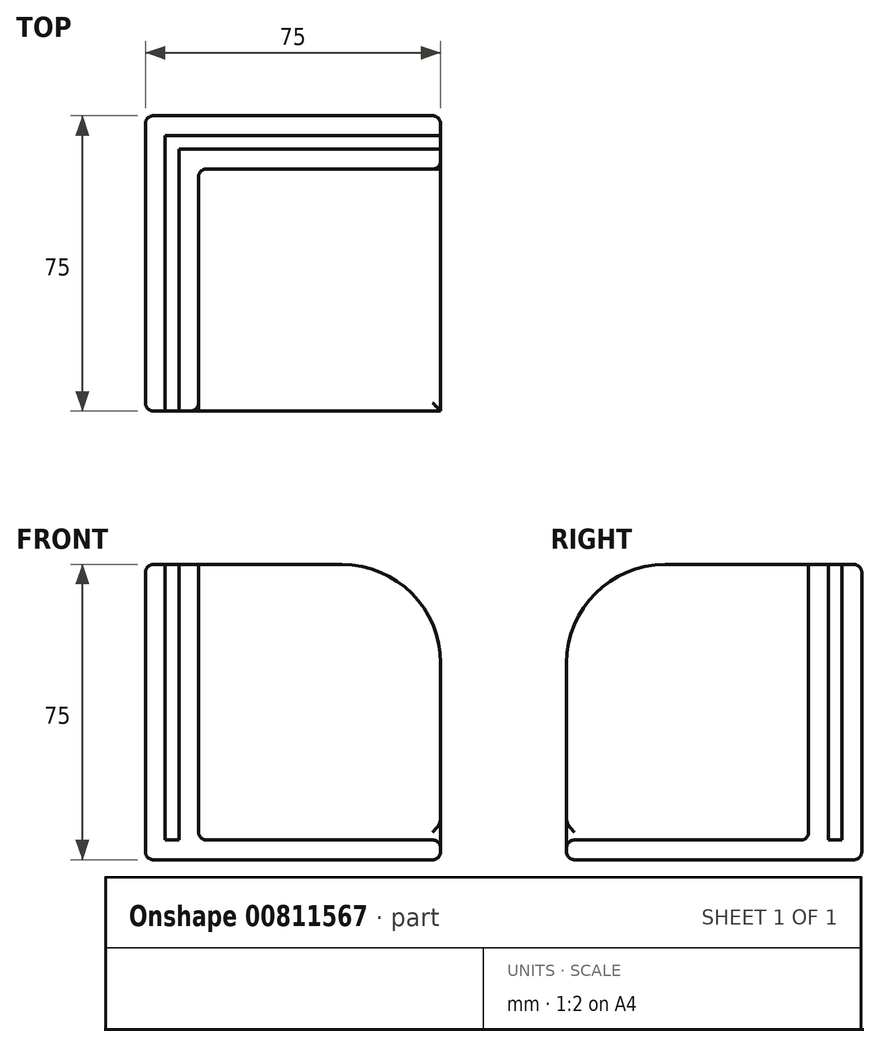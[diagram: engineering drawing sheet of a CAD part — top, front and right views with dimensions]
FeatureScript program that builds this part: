
annotation { "Feature Type Name" : "Feature", "Feature Type Description" : "" }
export const myFeature = defineFeature(function(context is Context, id is Id, definition is map)
    precondition{}
    {
        {
            var Q0;
            Q0=qCreatedBy(makeId("Top.planeOp"),FACE);
            var sketch = newSketch(context, id + "F0", { "sketchPlane" : qUnion([Q0])});
            skLineSegment(sketch, "E0.bottom", {"start": v(37.5, -37.5) * mm, "end": v(-37.5, -37.5) * mm});
            skLineSegment(sketch, "E0.top", {"start": v(37.5, 37.5) * mm, "end": v(-37.5, 37.5) * mm});
            skLineSegment(sketch, "E0.left", {"start": v(37.5, -37.5) * mm, "end": v(37.5, 37.5) * mm});
            skLineSegment(sketch, "E0.right", {"start": v(-37.5, -37.5) * mm, "end": v(-37.5, 37.5) * mm});
            skPoint(sketch, "E0.middle", {"position": v(0, 0) * mm});
            skSolve(sketch);
        }
        {
            var Q0;
            Q0 = qSketchRegion(id + "F0", true);
            extrude(context, id + "F1", {"entities" : qUnion([Q0]), "depth" : 5 * mm, "offsetDistance" : 25 * mm});
        }
        {
            var Q0;
            Q0=makeQuery(id+"F1.opExtrude","CAP_FACE",FACE,{"disambiguationData":[OSD([sQuery(id+"F0.wireOp",EDGE,"E0.bottom"),sQuery(id+"F0.wireOp",EDGE,"E0.top"),sQuery(id+"F0.wireOp",EDGE,"E0.left"),sQuery(id+"F0.wireOp",EDGE,"E0.right")])],"isStart":false});
            var sketch = newSketch(context, id + "F2", { "sketchPlane" : qUnion([Q0])});
            skLineSegment(sketch, "E1.bottom", {"start": v(-37.5, 37.5) * mm, "end": v(-32.5, 37.5) * mm});
            skLineSegment(sketch, "E1.top", {"start": v(-37.5, -37.5) * mm, "end": v(-32.5, -37.5) * mm});
            skLineSegment(sketch, "E1.left", {"start": v(-37.5, 37.5) * mm, "end": v(-37.5, -37.5) * mm});
            skLineSegment(sketch, "E1.right", {"start": v(-32.5, 37.5) * mm, "end": v(-32.5, -37.5) * mm});
            skLineSegment(sketch, "E2.bottom", {"start": v(-32.5, 37.5) * mm, "end": v(37.5, 37.5) * mm});
            skLineSegment(sketch, "E2.top", {"start": v(-32.5, 32.5) * mm, "end": v(37.5, 32.5) * mm});
            skLineSegment(sketch, "E2.left", {"start": v(-32.5, 37.5) * mm, "end": v(-32.5, 32.5) * mm});
            skLineSegment(sketch, "E2.right", {"start": v(37.5, 37.5) * mm, "end": v(37.5, 32.5) * mm});
            skSolve(sketch);
        }
        {
            var Q0;
            Q0 = qSketchRegion(id + "F2", true);
            extrude(context, id + "F3", {"entities" : qUnion([Q0]), "operationType" : NewBodyOperationType.ADD, "depth" : 70 * mm, "offsetDistance" : 25 * mm});
        }
        {
            var Q0;
            Q0=makeQuery(id+"F1.opExtrude","CAP_FACE",FACE,{"disambiguationData":[OSD([sQuery(id+"F0.wireOp",EDGE,"E0.bottom"),sQuery(id+"F0.wireOp",EDGE,"E0.top"),sQuery(id+"F0.wireOp",EDGE,"E0.left"),sQuery(id+"F0.wireOp",EDGE,"E0.right")])],"isStart":false});
            var sketch = newSketch(context, id + "F4", { "sketchPlane" : qUnion([Q0])});
            skLineSegment(sketch, "E3.bottom", {"start": v(-29, -37.5) * mm, "end": v(-24, -37.5) * mm});
            skLineSegment(sketch, "E3.top", {"start": v(-29, 29) * mm, "end": v(-24, 29) * mm});
            skLineSegment(sketch, "E3.left", {"start": v(-29, -37.5) * mm, "end": v(-29, 29) * mm});
            skLineSegment(sketch, "E3.right", {"start": v(-24, -37.5) * mm, "end": v(-24, 29) * mm});
            skLineSegment(sketch, "E4.bottom", {"start": v(-24, 29) * mm, "end": v(37.5, 29) * mm});
            skLineSegment(sketch, "E4.top", {"start": v(-24, 24) * mm, "end": v(37.5, 24) * mm});
            skLineSegment(sketch, "E4.left", {"start": v(-24, 29) * mm, "end": v(-24, 24) * mm});
            skLineSegment(sketch, "E4.right", {"start": v(37.5, 29) * mm, "end": v(37.5, 24) * mm});
            skSolve(sketch);
        }
        {
            var Q0;
            Q0 = qSketchRegion(id + "F4", true);
            var Q1;
            Q1=makeQuery(id+"F3.opExtrude","CAP_FACE",FACE,{"disambiguationData":[OSD([sQuery(id+"F2.wireOp",EDGE,"E1.bottom"),sQuery(id+"F2.wireOp",EDGE,"E1.top"),sQuery(id+"F2.wireOp",EDGE,"E1.left"),sQuery(id+"F2.wireOp",EDGE,"E1.right"),sQuery(id+"F2.wireOp",EDGE,"E2.bottom"),sQuery(id+"F2.wireOp",EDGE,"E2.top"),sQuery(id+"F2.wireOp",EDGE,"E2.right")])],"isStart":false});
            extrude(context, id + "F5", {"entities" : qUnion([Q0]), "operationType" : NewBodyOperationType.ADD, "endBound" : BoundingType.UP_TO_SURFACE, "depth" : 25 * mm, "endBoundEntityFace" : qUnion([Q1]), "offsetDistance" : 25 * mm});
        }
        {
            var Q0;
            Q0=makeQuery(id+"F3.opExtrude","CAP_EDGE",EDGE,{"disambiguationData":[OSD([sQuery(id+"F2.wireOp",EDGE,"E1.top")])],"isStart":false});
            var Q1;
            Q1=makeQuery(id+"F5.opExtrude","CAP_EDGE",EDGE,{"disambiguationData":[OSD([sQuery(id+"F4.wireOp",EDGE,"E3.bottom")])],"isStart":false});
            var Q2;
            Q2=makeQuery(id+"F5.opExtrude","CAP_EDGE",EDGE,{"disambiguationData":[OSD([sQuery(id+"F4.wireOp",EDGE,"E4.right")])],"isStart":false});
            var Q3;
            Q3=makeQuery(id+"F3.opExtrude","CAP_EDGE",EDGE,{"disambiguationData":[OSD([sQuery(id+"F2.wireOp",EDGE,"E2.right")])],"isStart":false});
            fillet(context, id + "F6", {"entities" : qUnion([Q0, Q1, Q2, Q3]), "radius" : 25 * mm, "tangentPropagation" : true, "allowEdgeOverflow" : false});
        }
        {
            var Q0;
            Q0=makeQuery(id+"F3.boolean.opBoolean","MERGE",FACE,{"derivedFrom":[makeQuery(id+"F1.opExtrude","SWEPT_FACE",FACE,{"disambiguationData":[OSD([sQuery(id+"F0.wireOp",EDGE,"E0.top")])]}),makeQuery(id+"F3.opExtrude","SWEPT_FACE",FACE,{"disambiguationData":[OSD([sQuery(id+"F2.wireOp",EDGE,"E1.bottom"),sQuery(id+"F2.wireOp",EDGE,"E2.bottom")])]})]});
            var Q1;
            Q1=makeQuery(id+"F1.opExtrude","CAP_FACE",FACE,{"disambiguationData":[OSD([sQuery(id+"F0.wireOp",EDGE,"E0.bottom"),sQuery(id+"F0.wireOp",EDGE,"E0.top"),sQuery(id+"F0.wireOp",EDGE,"E0.left"),sQuery(id+"F0.wireOp",EDGE,"E0.right")])],"isStart":true});
            var Q2;
            Q2=makeQuery(id+"F3.boolean.opBoolean","MERGE",FACE,{"derivedFrom":[makeQuery(id+"F1.opExtrude","SWEPT_FACE",FACE,{"disambiguationData":[OSD([sQuery(id+"F0.wireOp",EDGE,"E0.right")])]}),makeQuery(id+"F3.opExtrude","SWEPT_FACE",FACE,{"disambiguationData":[OSD([sQuery(id+"F2.wireOp",EDGE,"E1.left")])]})]});
            var Q3;
            {var subQ0=sQuery(id+"F0.wireOp",EDGE,"E0.left");var subQ1=sQuery(id+"F0.wireOp",EDGE,"E0.bottom");Q3=makeQuery(id+"F5.boolean.opBoolean","SPLIT",FACE,{"disambiguationData":[TD([makeQuery(id+"F5.opExtrude","SWEPT_FACE",FACE,{"disambiguationData":[OSD([sQuery(id+"F4.wireOp",EDGE,"E3.right")])]})])],"derivedFrom":makeQuery(id+"F1.opExtrude","CAP_FACE",FACE,{"disambiguationData":[OSD([subQ1,sQuery(id+"F0.wireOp",EDGE,"E0.top"),subQ0,sQuery(id+"F0.wireOp",EDGE,"E0.right")])],"isStart":false})});}
            var Q4;
            Q4=makeQuery(id+"F5.opExtrude","SWEPT_EDGE",EDGE,{"disambiguationData":[OSD([sQuery(id+"F4.wireOp",EDGE,"E3.right"),sQuery(id+"F4.wireOp",EDGE,"E4.top"),sQuery(id+"F4.wireOp",EDGE,"E4.left")])]});
            fillet(context, id + "F7", {"entities" : qUnion([Q0, Q1, Q2, Q3, Q4]), "radius" : 2 * mm, "tangentPropagation" : true, "allowEdgeOverflow" : false});
        }
    });
